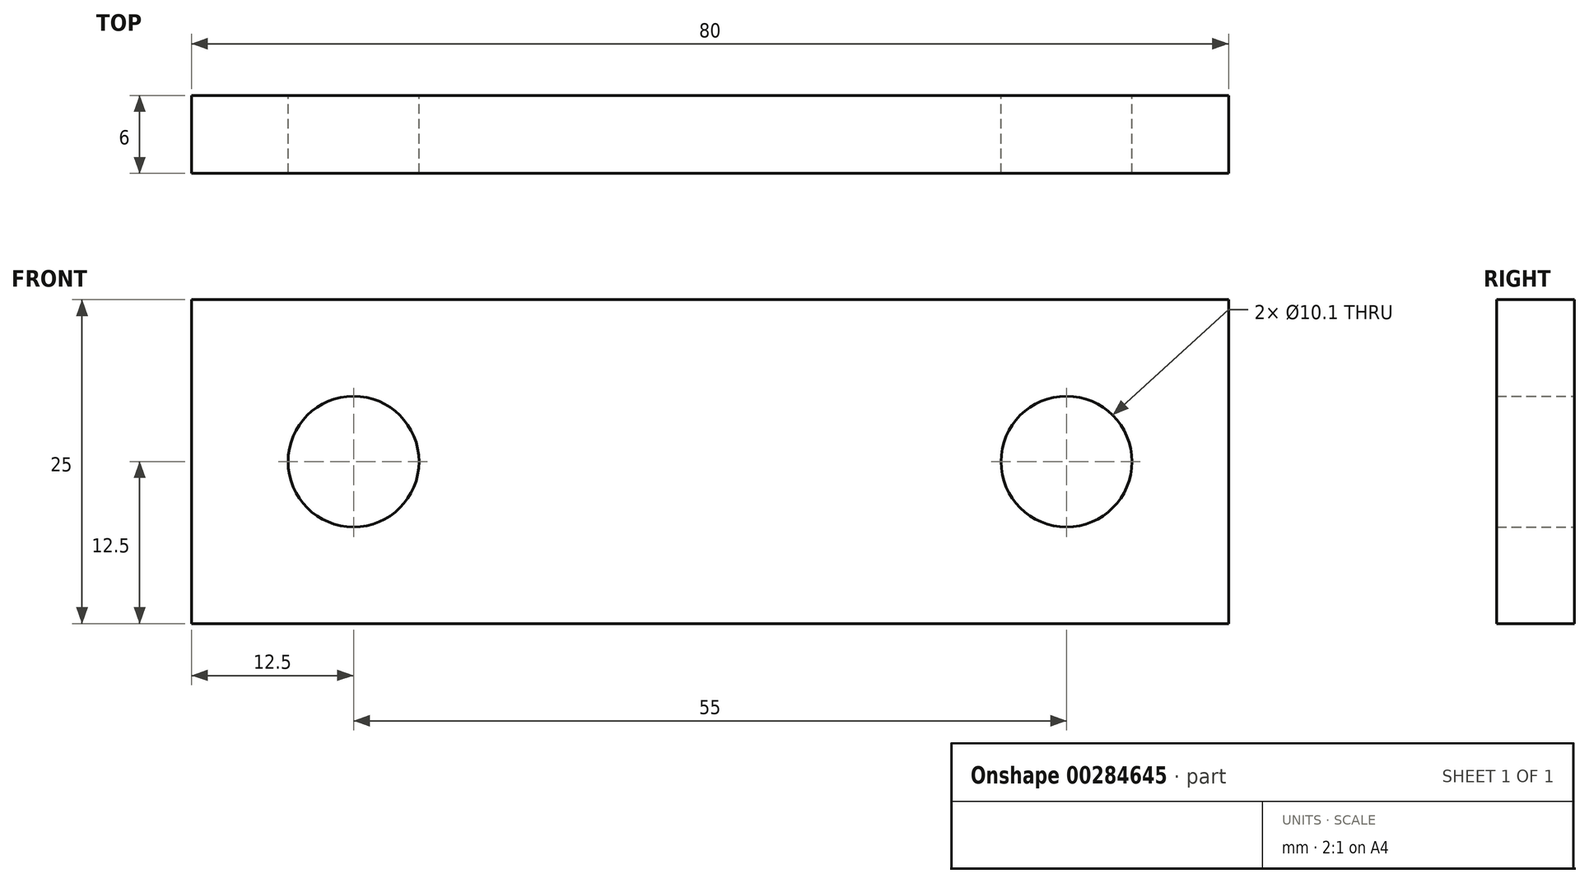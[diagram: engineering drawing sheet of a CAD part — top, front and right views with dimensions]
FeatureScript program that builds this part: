
annotation { "Feature Type Name" : "Feature", "Feature Type Description" : "" }
export const myFeature = defineFeature(function(context is Context, id is Id, definition is map)
    precondition{}
    {
        {
            var Q0;
            Q0=qCreatedBy(makeId("Front.planeOp"),FACE);
            var sketch = newSketch(context, id + "F0", { "sketchPlane" : qUnion([Q0])});
            skLineSegment(sketch, "E0.bottom", {"start": v(40, 12.5) * mm, "end": v(-40, 12.5) * mm});
            skLineSegment(sketch, "E0.top", {"start": v(40, -12.5) * mm, "end": v(-40, -12.5) * mm});
            skLineSegment(sketch, "E0.left", {"start": v(40, 12.5) * mm, "end": v(40, -12.5) * mm});
            skLineSegment(sketch, "E0.right", {"start": v(-40, 12.5) * mm, "end": v(-40, -12.5) * mm});
            skPoint(sketch, "E0.middle", {"position": v(0, 0) * mm});
            skCircle(sketch, "E1", {"center": v(-27.5, 0) * mm, "radius": 5.05 * mm});
            skPoint(sketch, "E1.centerSnap0", {"position": v(-40, 0) * mm});
            skCircle(sketch, "E2", {"center": v(27.5, 0) * mm, "radius": 5.05 * mm});
            skSolve(sketch);
        }
        {
            var Q0;
            Q0=makeQuery(id+"F0.imprint","IMPRINT",FACE,{"disambiguationData":[TD([[makeQuery(id+"F0.imprint","IMPRINT",EDGE,{"derivedFrom":sQuery(id+"F0.wireOp",EDGE,"E0.bottom")}),1.0]])]});
            extrude(context, id + "F1", {"entities" : qUnion([Q0]), "depth" : 6 * mm});
        }
    });
